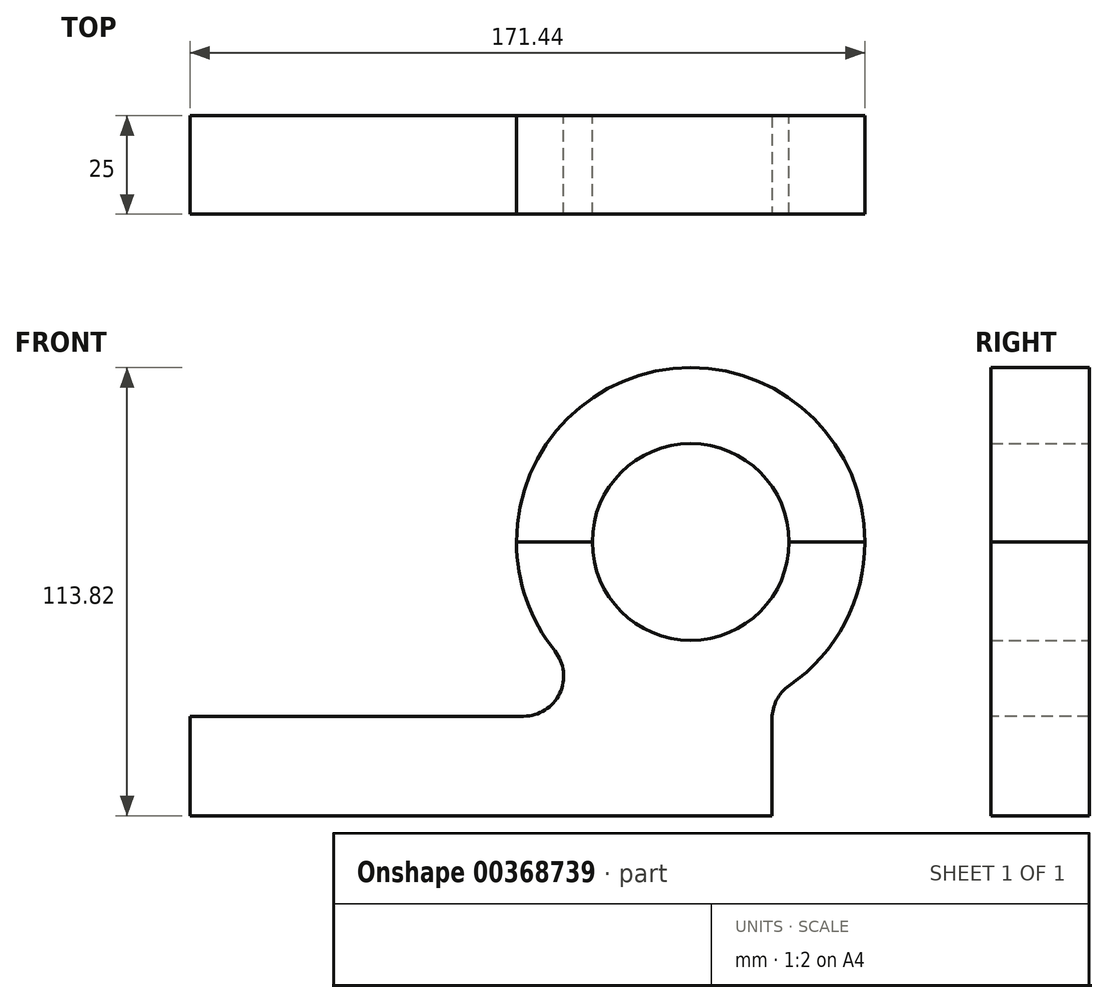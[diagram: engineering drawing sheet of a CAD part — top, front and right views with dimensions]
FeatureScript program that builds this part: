
annotation { "Feature Type Name" : "Feature", "Feature Type Description" : "" }
export const myFeature = defineFeature(function(context is Context, id is Id, definition is map)
    precondition{}
    {
        {
            var Q0;
            Q0=qCreatedBy(makeId("Front.planeOp"),FACE);
            var sketch = newSketch(context, id + "F0", { "sketchPlane" : qUnion([Q0])});
            skCircle(sketch, "E0", {"center": v(0, 0) * mm, "radius": 25 * mm});
            skCircle(sketch, "E1.0", {"center": v(0, 0) * mm, "radius": 44.27 * mm});
            skLineSegment(sketch, "E2", {"start": v(0, -44.27) * mm, "end": v(-127.17, -44.27) * mm});
            skLineSegment(sketch, "E3", {"start": v(-127.17, -44.27) * mm, "end": v(-127.17, -69.55) * mm});
            skLineSegment(sketch, "E4", {"start": v(-127.17, -69.55) * mm, "end": v(20.68, -69.55) * mm});
            skLineSegment(sketch, "E5", {"start": v(20.68, -69.55) * mm, "end": v(20.68, -39.14) * mm});
            skLineSegment(sketch, "E6", {"start": v(-44.27, 0) * mm, "end": v(44.27, 0) * mm});
            skSolve(sketch);
        }
        {
            var Q0;
            {var subQ0=sQuery(id+"F0.wireOp",EDGE,"dcc4223b-3dc6-46eb-9acf-0d096ac43793");Q0=makeQuery(id+"F0.imprint","IMPRINT",FACE,{"disambiguationData":[TD([[makeQuery(id+"F0.imprint","IMPRINT",EDGE,{"derivedFrom":subQ0}),1.0]])]});}
            var Q1;
            {var subQ0=sQuery(id+"F0.wireOp",EDGE,"E2");Q1=makeQuery(id+"F0.imprint","IMPRINT",FACE,{"disambiguationData":[TD([[makeQuery(id+"F0.imprint","IMPRINT",EDGE,{"derivedFrom":subQ0}),1.0]])]});}
            var Q2;
            {var subQ2=sQuery(id+"F0.wireOp",EDGE,"E6");var subQ6=sQuery(id+"F0.wireOp",EDGE,"E0");var subQ7=makeQuery(id+"F0.imprint","INTERSECT",VERTEX,{"disambiguationData":[OD(0.0)],"derivedFrom":[subQ6,subQ2]});Q2=makeQuery(id+"F0.imprint","IMPRINT",FACE,{"disambiguationData":[TD([[makeQuery(id+"F0.imprint","IMPRINT",EDGE,{"disambiguationData":[TD([[subQ7,-1.0]])],"derivedFrom":subQ6}),-1.0]])]});}
            extrude(context, id + "F1", {"entities" : qUnion([Q0, Q1, Q2]), "depth" : 25 * mm});
        }
        {
            var Q0;
            {var subQ0=sQuery(id+"F0.wireOp",EDGE,"E6");var subQ1=sQuery(id+"F0.wireOp",EDGE,"E0");var subQ2=makeQuery(id+"F0.imprint","INTERSECT",VERTEX,{"disambiguationData":[OD(0.0)],"derivedFrom":[subQ1,subQ0]});Q0=makeQuery(id+"F0.imprint","IMPRINT",FACE,{"disambiguationData":[TD([[makeQuery(id+"F0.imprint","IMPRINT",EDGE,{"disambiguationData":[TD([[subQ2,1.0]])],"derivedFrom":subQ1}),-1.0]])]});}
            extrude(context, id + "F2", {"entities" : qUnion([Q0]), "depth" : 25 * mm});
        }
        {
            var Q0;
            Q0=makeQuery(id+"F1.opExtrude","SWEPT_EDGE",EDGE,{"disambiguationData":[OSD([sQuery(id+"F0.wireOp",EDGE,"E1.0"),sQuery(id+"F0.wireOp",EDGE,"E2")])]});
            var Q1;
            Q1=makeQuery(id+"F1.opExtrude","SWEPT_EDGE",EDGE,{"disambiguationData":[OSD([sQuery(id+"F0.wireOp",EDGE,"E1.0"),sQuery(id+"F0.wireOp",EDGE,"E5")])]});
            fillet(context, id + "F3", {"entities" : qUnion([Q0, Q1]), "radius" : 10.18 * mm, "tangentPropagation" : true, "allowEdgeOverflow" : false});
        }
    });
